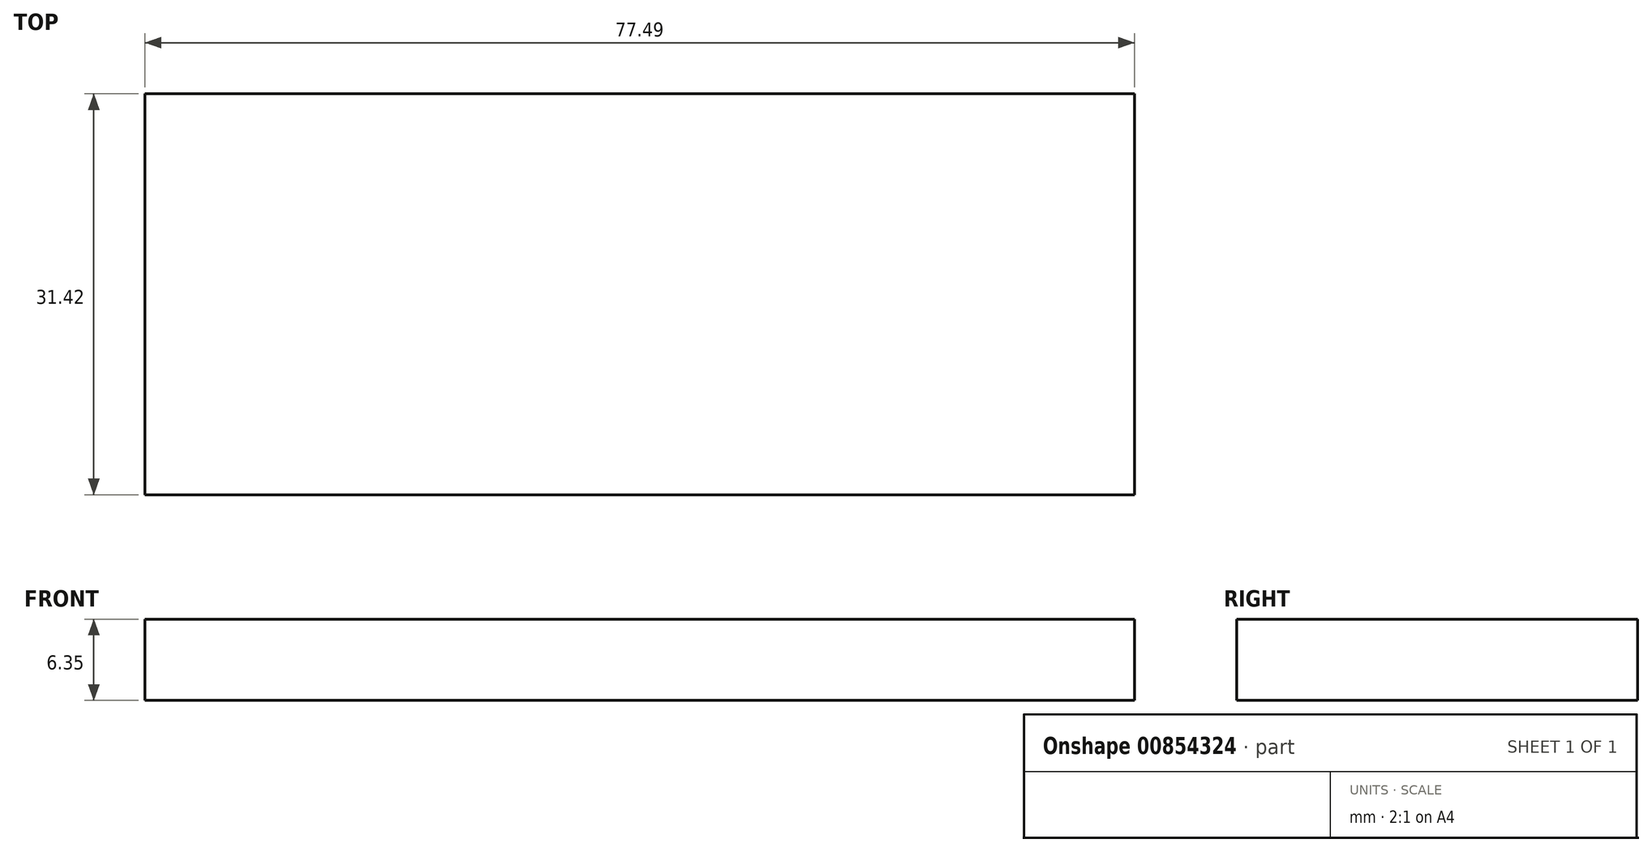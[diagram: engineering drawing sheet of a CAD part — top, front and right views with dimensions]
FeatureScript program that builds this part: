
annotation { "Feature Type Name" : "Feature", "Feature Type Description" : "" }
export const myFeature = defineFeature(function(context is Context, id is Id, definition is map)
    precondition{}
    {
        {
            var Q0;
            Q0=qCreatedBy(makeId("Top.planeOp"),FACE);
            var sketch = newSketch(context, id + "F0", { "sketchPlane" : qUnion([Q0])});
            skLineSegment(sketch, "E0.bottom", {"start": v(0, 0) * mm, "end": v(77.5, 0) * mm});
            skLineSegment(sketch, "E0.top", {"start": v(0, 31.42) * mm, "end": v(77.5, 31.42) * mm});
            skLineSegment(sketch, "E0.left", {"start": v(0, 0) * mm, "end": v(0, 31.42) * mm});
            skLineSegment(sketch, "E0.right", {"start": v(77.5, 0) * mm, "end": v(77.5, 31.42) * mm});
            skSolve(sketch);
        }
        {
            var Q0;
            Q0 = qSketchRegion(id + "F0", true);
            extrude(context, id + "F1", {"entities" : qUnion([Q0]), "depth" : 6.35 * mm, "offsetDistance" : 25.4 * mm});
        }
    });
